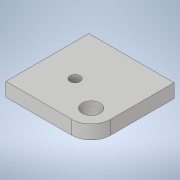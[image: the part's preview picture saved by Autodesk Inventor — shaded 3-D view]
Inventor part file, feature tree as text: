
AUTODESK INVENTOR PART (.ipt)
format: ipt  version: 2021 (Build 250183000, 183)  size: 117,248 bytes
history: native  units: mm
features: sketch x5, hole x2, other x1, extrude x1, fillet x1
ambient origin geometry x8: Origin, YZ Plane, XZ Plane, XY Plane, X Axis, Y Axis, Z Axis, Center Point
bodies: Body1 (feature_tree)
feature tree (10):
  other  "Твердое тело1"
  extrude  "Выдавливание1"  Depth=185.0mm
  fillet  "Сопряжение1"  Radius=180.0mm
  hole  "Отверстие5"  [1 undecoded]
  hole  "Отверстие6"  [1 undecoded]
  sketch  "Эскиз1"
  sketch  "Эскиз3"
  sketch  "Эскиз4"
  sketch  "Эскиз7"
  sketch  "Эскиз8"
note: 2 required parameter values undecoded (feature->parameter linkage not recoverable at this tier; creation-order binding heuristic only, values carry confidence <= 0.55)
